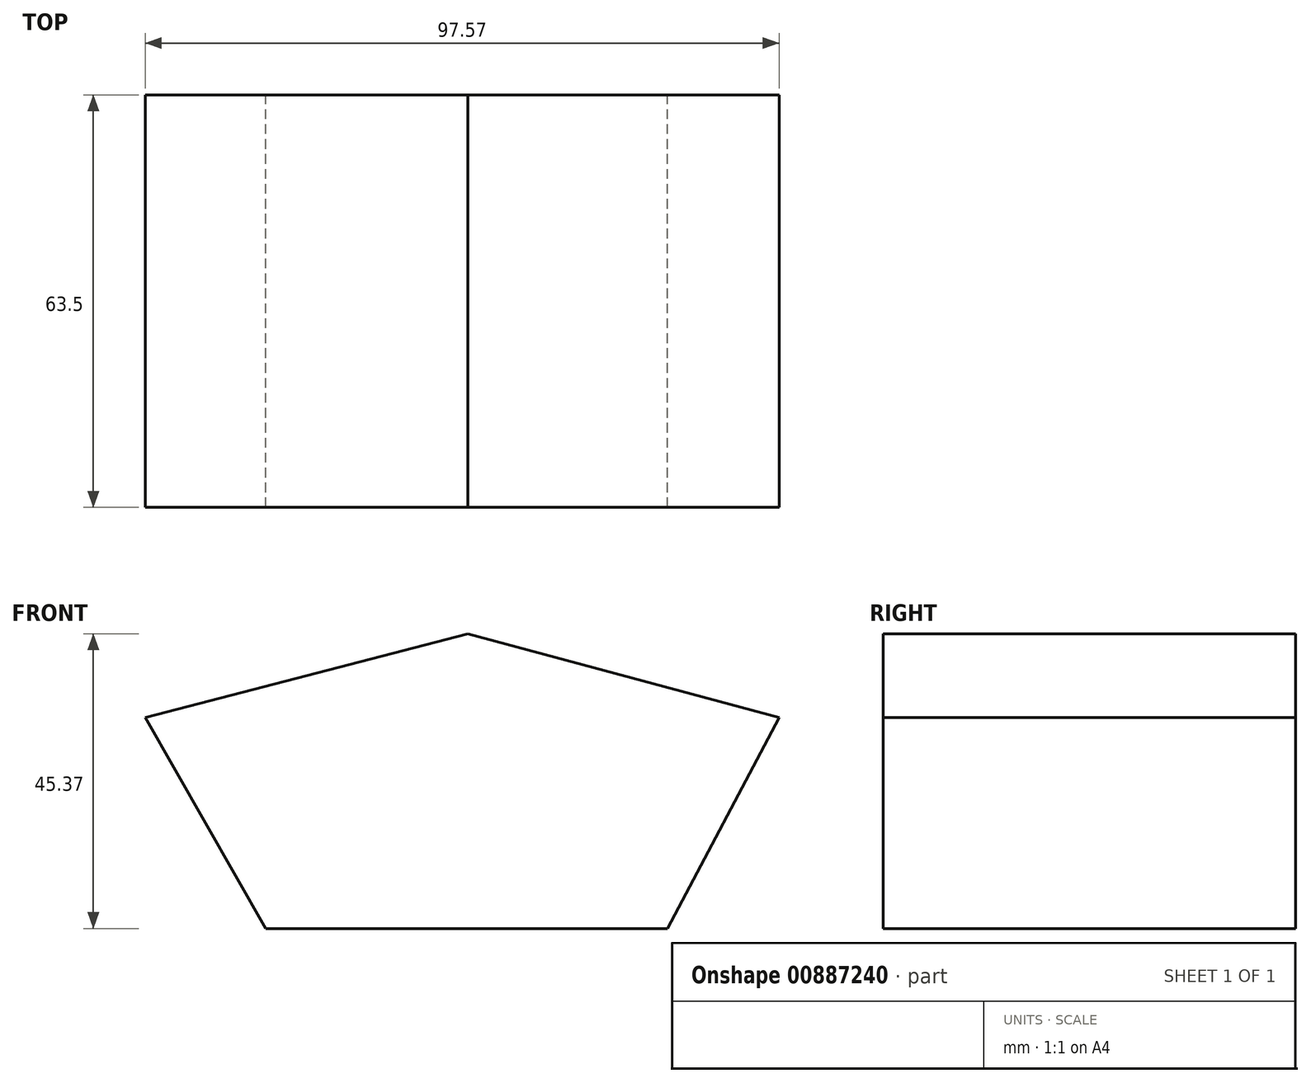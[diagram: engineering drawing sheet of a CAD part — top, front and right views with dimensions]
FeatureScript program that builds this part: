
annotation { "Feature Type Name" : "Feature", "Feature Type Description" : "" }
export const myFeature = defineFeature(function(context is Context, id is Id, definition is map)
    precondition{}
    {
        {
            var Q0;
            Q0=qCreatedBy(makeId("Front.planeOp"),FACE);
            var sketch = newSketch(context, id + "F0", { "sketchPlane" : qUnion([Q0])});
            skLineSegment(sketch, "E0", {"start": v(30.68, -32.5) * mm, "end": v(-31.13, -32.5) * mm});
            skLineSegment(sketch, "E1", {"start": v(-31.13, -32.5) * mm, "end": v(-49.69, 0) * mm});
            skLineSegment(sketch, "E2", {"start": v(-49.69, 0) * mm, "end": v(0, 12.88) * mm});
            skLineSegment(sketch, "E3", {"start": v(0, 12.88) * mm, "end": v(47.88, 0) * mm});
            skLineSegment(sketch, "E4", {"start": v(47.88, 0) * mm, "end": v(30.68, -32.5) * mm});
            skSolve(sketch);
        }
        {
            var Q0;
            Q0=makeQuery(id+"F0.imprint","IMPRINT",FACE,{"disambiguationData":[TD([[makeQuery(id+"F0.imprint","IMPRINT",EDGE,{"derivedFrom":sQuery(id+"F0.wireOp",EDGE,"E0")}),-1.0]])]});
            extrude(context, id + "F1", {"entities" : qUnion([Q0]), "depth" : 63.5 * mm, "offsetDistance" : 25.4 * mm});
        }
        {
            var Q0;
            Q0=makeQuery(id+"F1.opExtrude","SWEPT_FACE",FACE,{"disambiguationData":[OSD([sQuery(id+"F0.wireOp",EDGE,"E2")])]});
            var sketch = newSketch(context, id + "F2", { "sketchPlane" : qUnion([Q0])});
            skCircle(sketch, "E5", {"center": v(-21.63, -29.82) * mm, "radius": 8.74 * mm});
            skSolve(sketch);
        }
        {
            var Q0;
            Q0=sQuery(id+"F2.wireOp",EDGE,"E5");
            extrude(context, id + "F3", {"bodyType" : ToolBodyType.SURFACE, "surfaceEntities" : qUnion([Q0]), "oppositeDirection" : true, "depth" : 25.4 * mm, "offsetDistance" : 25.4 * mm});
        }
    });
